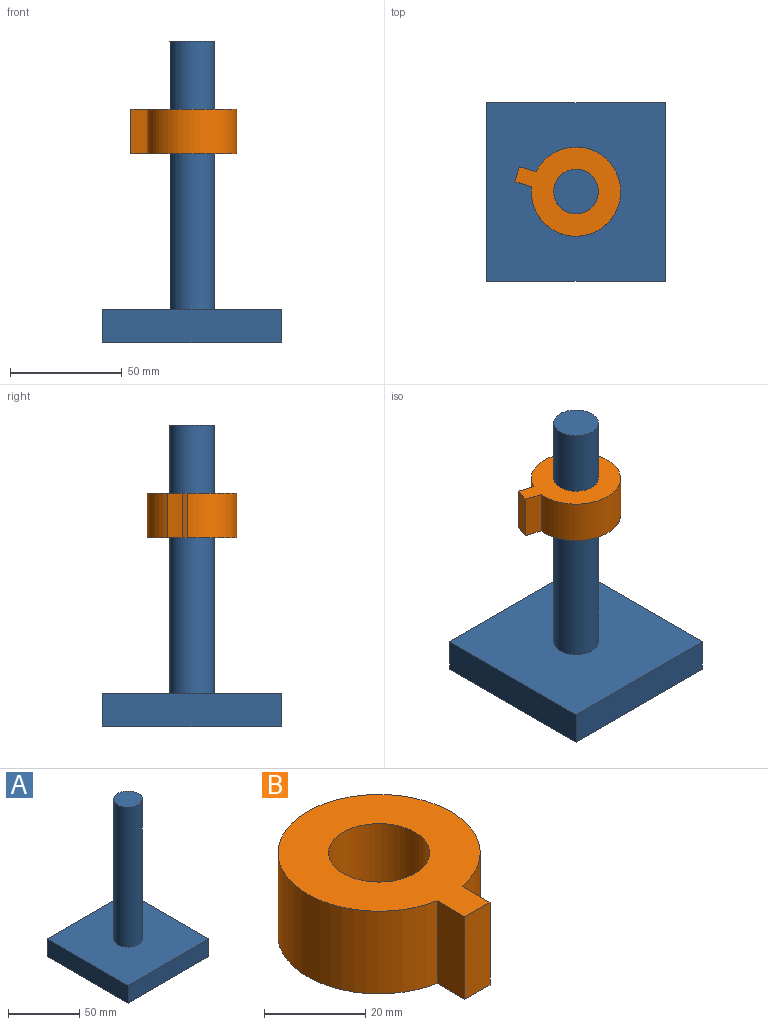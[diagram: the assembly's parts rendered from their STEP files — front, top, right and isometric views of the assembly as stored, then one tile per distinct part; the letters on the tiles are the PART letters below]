
ASSEMBLY  parts=2 mates=1
PART A: 8 faces, bbox 80x80x135 mm
  f0: plane 80x15mm, normal (1,0,0), area 1200mm2, adj f1,f3,f4,f5
  f1: plane 80x15mm, normal (0,1,0), area 1200mm2, adj f0,f2,f4,f5
  f2: plane 80x15mm, normal (-1,0,0), area 1200mm2, adj f1,f3,f4,f5
  f3: plane 80x15mm, normal (0,-1,0), area 1200mm2, adj f0,f2,f4,f5
  f4: plane 80x80mm, normal (0,0,1), area 6085.8mm2, adj f0,f1,f2,f3,f6
  f5: plane 80x80mm, normal (0,0,-1), area 6400mm2, adj f0,f1,f2,f3
  f6: cylinder r=10mm len=120mm, axis (0,0,-1), area 7539.8mm2, adj f4,f7
  f7: plane 20x20mm, normal (0,0,1), area 314.2mm2, adj f6
PART B: 7 faces, bbox 40x47.5x20 mm
  f0: cylinder r=20mm len=40mm, axis (0,0,-1), area 2372.5mm2, adj f2,f3,f4,f5
  f1: cylinder r=10mm len=20mm, axis (0,0,-1), area 1256.6mm2, adj f2,f3
  f2: plane 47.5x40mm, normal (0,0,1), area 995.7mm2, adj f0,f1,f4,f5,f6
  f3: plane 47.5x40mm, normal (0,0,-1), area 995.7mm2, adj f0,f1,f4,f5,f6
  f4: plane 20x7.81mm, normal (-1,0,0), area 156.2mm2, adj f0,f2,f3,f6
  f5: plane 20x7.81mm, normal (1,0,0), area 156.2mm2, adj f0,f2,f3,f6
  f6: plane 20x7mm, normal (0,-1,0), area 140mm2, adj f2,f3,f4,f5
PLACE A t=(-99.8,-15.97,-5.02)mm fixed
PLACE B rot(axis=(0,0,-1),106.5deg) t=(-99.8,-15.97,79.55)mm
MATE cylindrical B.f0 <-> A.f6  axis (0,0,-1) through (-99.8,-15.97,99.55)mm
